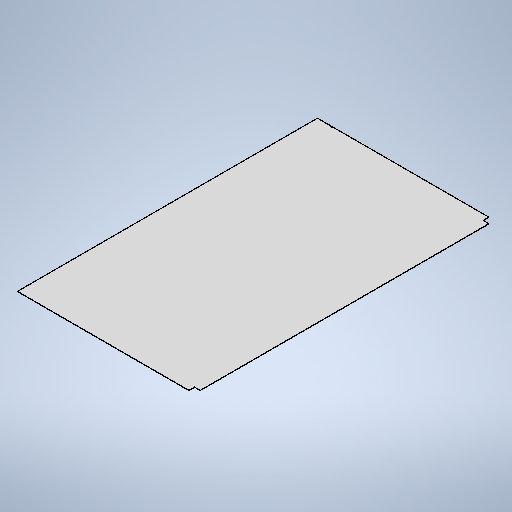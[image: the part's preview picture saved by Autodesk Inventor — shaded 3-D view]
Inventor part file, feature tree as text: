
AUTODESK INVENTOR PART (.ipt)
format: ipt  version: 2025.3 (Build 293356000, 356)  size: 283,136 bytes
history: native  units: mm
features: other x3, sketch x2, sheet_metal_op x1, projected_geometry x1
ambient origin geometry x8: Origin, YZ Plane, XZ Plane, XY Plane, X Axis, Y Axis, Z Axis, Center Point
bodies: Solid1 (feature_tree)
feature tree (7):
  sheet_metal_op  "Face1"
  sketch  "Sketch1"  dims[d2=3.0mm]
  other  "Plate1"
  sketch  "Sketch5"  dims[d22=1240.0mm d23=2100.0mm d24=40.0mm d25=40.0mm d34=2.0mm d35=5.0mm d36=0.5mm d37=100.0mm d38=3.0mm d39=0.0mm d40=3.0mm d41=2.0mm d42=5.0mm d43=3.0mm d44=5.0mm]
  projected_geometry  "Projected Loop2"
  other  "Cut1"
  other  "Definition1"
